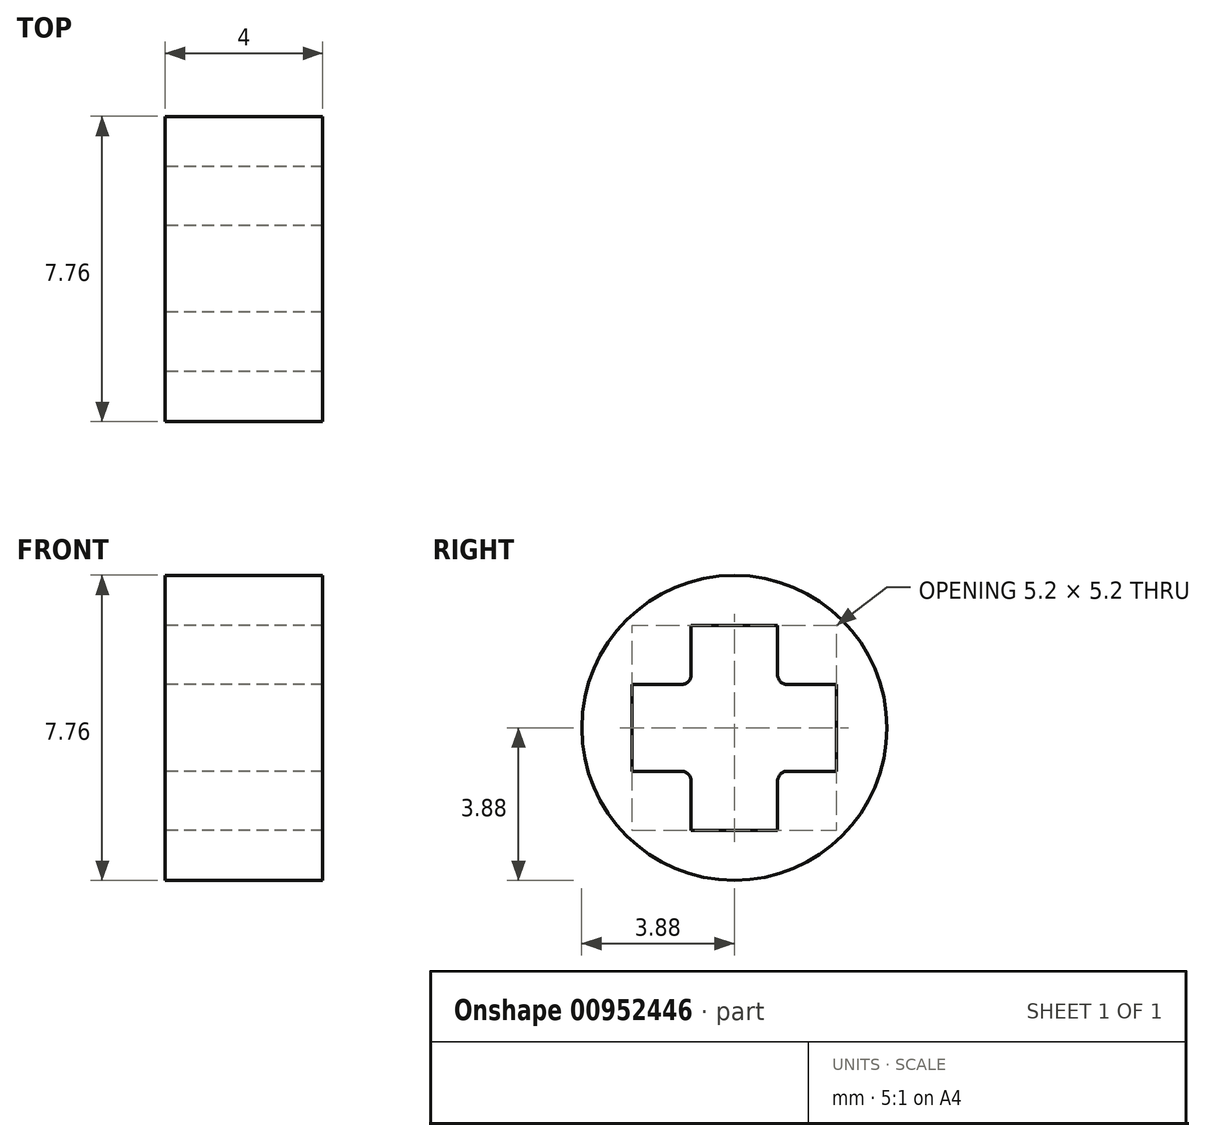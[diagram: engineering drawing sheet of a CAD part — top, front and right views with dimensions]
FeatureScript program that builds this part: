
annotation { "Feature Type Name" : "Feature", "Feature Type Description" : "" }
export const myFeature = defineFeature(function(context is Context, id is Id, definition is map)
    precondition{}
    {
        {
            var Q0;
            Q0=qCreatedBy(makeId("Right.planeOp"),FACE);
            var sketch = newSketch(context, id + "F0", { "sketchPlane" : qUnion([Q0])});
            skLineSegment(sketch, "E0.bottom", {"start": v(1.1, 2.6) * mm, "end": v(-1.1, 2.6) * mm});
            skLineSegment(sketch, "E0.top", {"start": v(1.1, -2.6) * mm, "end": v(-1.1, -2.6) * mm});
            skLineSegment(sketch, "E0.left", {"start": v(1.1, 2.6) * mm, "end": v(1.1, -2.6) * mm});
            skLineSegment(sketch, "E0.right", {"start": v(-1.1, 2.6) * mm, "end": v(-1.1, -2.6) * mm});
            skPoint(sketch, "E0.middle", {"position": v(0, 0) * mm});
            skLineSegment(sketch, "E1.bottom", {"start": v(-2.6, -1.1) * mm, "end": v(2.6, -1.1) * mm});
            skLineSegment(sketch, "E1.top", {"start": v(-2.6, 1.1) * mm, "end": v(2.6, 1.1) * mm});
            skLineSegment(sketch, "E1.left", {"start": v(-2.6, -1.1) * mm, "end": v(-2.6, 1.1) * mm});
            skLineSegment(sketch, "E1.right", {"start": v(2.6, -1.1) * mm, "end": v(2.6, 1.1) * mm});
            skCircle(sketch, "E2", {"center": v(0, 0) * mm, "radius": 3.88 * mm});
            skSolve(sketch);
        }
        {
            var Q0;
            {var subQ8=sQuery(id+"F0.wireOp",EDGE,"E0.bottom");Q0=makeQuery(id+"F0.imprint","IMPRINT",FACE,{"disambiguationData":[TD([[makeQuery(id+"F0.imprint","IMPRINT",EDGE,{"derivedFrom":subQ8}),-1.0]])]});}
            extrude(context, id + "F1", {"entities" : qUnion([Q0]), "depth" : 4 * mm, "offsetDistance" : 25.4 * mm});
        }
        {
            var Q0;
            Q0=makeQuery(id+"F1.opExtrude","SWEPT_EDGE",EDGE,{"disambiguationData":[OSD([sQuery(id+"F0.wireOp",EDGE,"E0.left"),sQuery(id+"F0.wireOp",EDGE,"E1.bottom")])]});
            var Q1;
            Q1=makeQuery(id+"F1.opExtrude","SWEPT_EDGE",EDGE,{"disambiguationData":[OSD([sQuery(id+"F0.wireOp",EDGE,"E0.left"),sQuery(id+"F0.wireOp",EDGE,"E1.top")])]});
            var Q2;
            Q2=makeQuery(id+"F1.opExtrude","SWEPT_EDGE",EDGE,{"disambiguationData":[OSD([sQuery(id+"F0.wireOp",EDGE,"E0.right"),sQuery(id+"F0.wireOp",EDGE,"E1.bottom")])]});
            var Q3;
            Q3=makeQuery(id+"F1.opExtrude","SWEPT_EDGE",EDGE,{"disambiguationData":[OSD([sQuery(id+"F0.wireOp",EDGE,"E0.right"),sQuery(id+"F0.wireOp",EDGE,"E1.top")])]});
            fillet(context, id + "F2", {"entities" : qUnion([Q0, Q1, Q2, Q3]), "radius" : 0.25 * mm, "tangentPropagation" : true, "allowEdgeOverflow" : false});
        }
    });
